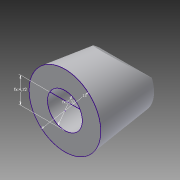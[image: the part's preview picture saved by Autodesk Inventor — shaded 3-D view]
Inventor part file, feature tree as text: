
AUTODESK INVENTOR PART (.ipt)
format: ipt  version: 2013 (Build 170138000, 138)  size: 102,400 bytes
history: native  units: mm
features: extrude x4, sketch x2, projected_geometry x1
ambient origin geometry x8: Origin, YZ Plane, XZ Plane, XY Plane, X Axis, Y Axis, Z Axis, Center Point
bodies: Solid1 (feature_tree)
feature tree (7):
  sketch  "Sketch1"  dims[d0=6.32mm d2=13.0mm]
  extrude  "Extrusion1"  Depth=13.0mm
  extrude  "Extrusion2"  Depth=2.7mm TaperAngle=0.0deg
  extrude  "Extrusion3"  Depth=4.72mm
  extrude  "Extrusion5"  Depth=9.7mm TaperAngle=0.0deg
  sketch  "Sketch3"  dims[d3=11.0mm d4=-1.22173mm d5=2.7mm d6=0.0mm d7=4.72mm d8=9.7mm d9=0.0mm d12=1.2mm d13=7.0mm d14=10.0mm d15=0.0mm]
  projected_geometry  "Project Cut Edges1"
